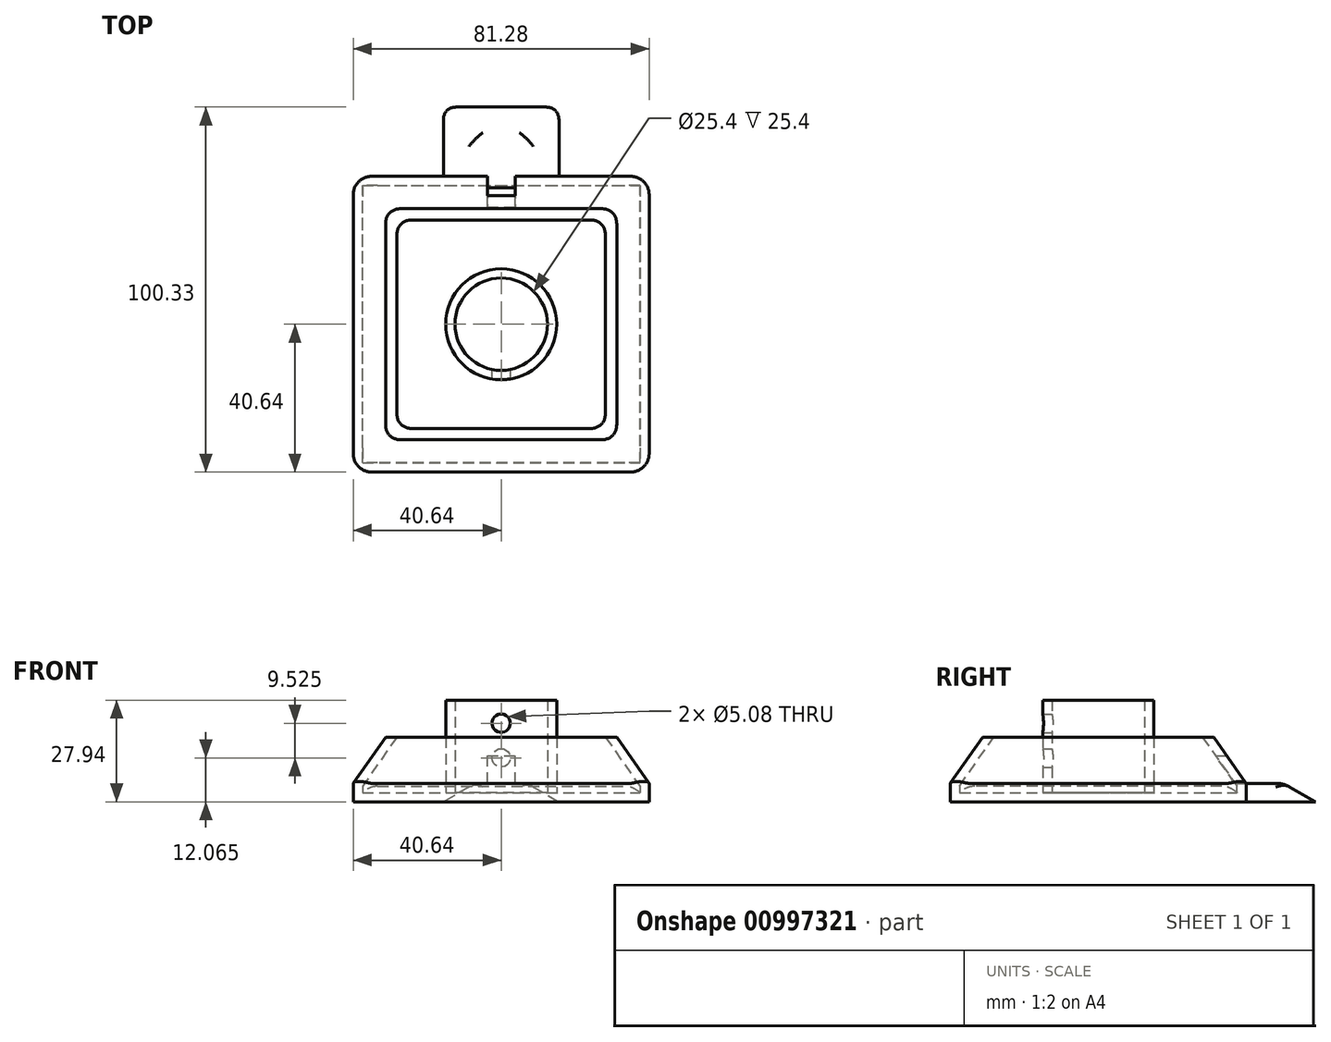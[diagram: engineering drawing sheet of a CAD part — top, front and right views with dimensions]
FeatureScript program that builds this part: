
annotation { "Feature Type Name" : "Feature", "Feature Type Description" : "" }
export const myFeature = defineFeature(function(context is Context, id is Id, definition is map)
    precondition{}
    {
        {
            var Q0;
            Q0=qCreatedBy(makeId("Top.planeOp"),FACE);
            var sketch = newSketch(context, id + "F0", { "sketchPlane" : qUnion([Q0])});
            skLineSegment(sketch, "E0.bottom", {"start": v(40.64, 40.64) * mm, "end": v(-40.64, 40.64) * mm});
            skLineSegment(sketch, "E0.top", {"start": v(40.64, -40.64) * mm, "end": v(-40.64, -40.64) * mm});
            skLineSegment(sketch, "E0.left", {"start": v(40.64, 40.64) * mm, "end": v(40.64, -40.64) * mm});
            skLineSegment(sketch, "E0.right", {"start": v(-40.64, 40.64) * mm, "end": v(-40.64, -40.64) * mm});
            skPoint(sketch, "E0.middle", {"position": v(0, 0) * mm});
            skSolve(sketch);
        }
        {
            var Q0;
            Q0 = qSketchRegion(id + "F0", true);
            extrude(context, id + "F1", {"entities" : qUnion([Q0]), "depth" : 5.08 * mm, "offsetDistance" : 25.4 * mm});
        }
        {
            var Q0;
            Q0=makeQuery(id+"F1.opExtrude","CAP_FACE",FACE,{"disambiguationData":[OSD([sQuery(id+"F0.wireOp",EDGE,"E0.bottom"),sQuery(id+"F0.wireOp",EDGE,"E0.top"),sQuery(id+"F0.wireOp",EDGE,"E0.left"),sQuery(id+"F0.wireOp",EDGE,"E0.right")])],"isStart":false});
            extrude(context, id + "F2", {"entities" : qUnion([Q0]), "operationType" : NewBodyOperationType.ADD, "depth" : 12.7 * mm, "offsetDistance" : 25.4 * mm, "hasDraft" : true, "draftAngle" : 35 * degree, "draftPullDirection" : true});
        }
        {
            var Q0;
            Q0=makeQuery(id+"F2.opExtrude","CAP_FACE",FACE,{"disambiguationData":[OSD([sQuery(id+"F0.wireOp",EDGE,"E0.bottom"),sQuery(id+"F0.wireOp",EDGE,"E0.top"),sQuery(id+"F0.wireOp",EDGE,"E0.left"),sQuery(id+"F0.wireOp",EDGE,"E0.right")])],"isStart":false});
            var Q1;
            Q1=makeQuery(id+"F1.opExtrude","CAP_FACE",FACE,{"disambiguationData":[OSD([sQuery(id+"F0.wireOp",EDGE,"E0.bottom"),sQuery(id+"F0.wireOp",EDGE,"E0.top"),sQuery(id+"F0.wireOp",EDGE,"E0.left"),sQuery(id+"F0.wireOp",EDGE,"E0.right")])],"isStart":true});
            shell(context, id + "F3", {"entities" : qUnion([Q0, Q1]), "thickness" : 2.54 * mm});
        }
        {
            var Q0;
            Q0=makeQuery(id+"F1.opExtrude","CAP_FACE",FACE,{"disambiguationData":[OSD([sQuery(id+"F0.wireOp",EDGE,"E0.bottom"),sQuery(id+"F0.wireOp",EDGE,"E0.top"),sQuery(id+"F0.wireOp",EDGE,"E0.left"),sQuery(id+"F0.wireOp",EDGE,"E0.right")])],"isStart":true});
            var sketch = newSketch(context, id + "F4", { "sketchPlane" : qUnion([Q0])});
            skLineSegment(sketch, "E1.0.0", {"start": v(40.64, 40.64) * mm, "end": v(-40.64, 40.64) * mm});
            skLineSegment(sketch, "E1.0.1", {"start": v(-40.64, 40.64) * mm, "end": v(-40.64, -40.64) * mm});
            skLineSegment(sketch, "E1.0.2", {"start": v(-40.64, -40.64) * mm, "end": v(40.64, -40.64) * mm});
            skLineSegment(sketch, "E1.0.3", {"start": v(40.64, -40.64) * mm, "end": v(40.64, 40.64) * mm});
            skSolve(sketch);
        }
        {
            var Q0;
            Q0 = qSketchRegion(id + "F4", true);
            extrude(context, id + "F5", {"entities" : qUnion([Q0]), "operationType" : NewBodyOperationType.ADD, "oppositeDirection" : true, "depth" : 2.54 * mm, "offsetDistance" : 25.4 * mm});
        }
        {
            var Q0;
            Q0=makeQuery(id+"F5.opExtrude","CAP_FACE",FACE,{"disambiguationData":[OSD([sQuery(id+"F4.wireOp",EDGE,"E1.0.0"),sQuery(id+"F4.wireOp",EDGE,"E1.0.1"),sQuery(id+"F4.wireOp",EDGE,"E1.0.2"),sQuery(id+"F4.wireOp",EDGE,"E1.0.3")])],"isStart":false});
            var sketch = newSketch(context, id + "F6", { "sketchPlane" : qUnion([Q0])});
            skCircle(sketch, "E2", {"center": v(0, 0) * mm, "radius": 12.7 * mm});
            skCircle(sketch, "E3.0", {"center": v(0, 0) * mm, "radius": 15.24 * mm});
            skSolve(sketch);
        }
        {
            var Q0;
            Q0 = qSketchRegion(id + "F6", true);
            extrude(context, id + "F7", {"entities" : qUnion([Q0]), "operationType" : NewBodyOperationType.ADD, "depth" : 25.4 * mm, "offsetDistance" : 25.4 * mm});
        }
        {
            var Q0;
            Q0=makeQuery(id+"F1.opExtrude","SWEPT_FACE",FACE,{"disambiguationData":[OSD([sQuery(id+"F0.wireOp",EDGE,"E0.bottom")])]});
            cPlane(context, id + "F8", {"entities" : qUnion([Q0]), "cplaneType" : CPlaneType.OFFSET, "offset" : 40.64 * mm, "oppositeDirection" : true, "width" : 152.4 * mm, "height" : 152.4 * mm});
        }
        {
            var Q0;
            Q0=qCreatedBy(id+"F8.planeOp",FACE);
            var sketch = newSketch(context, id + "F9", { "sketchPlane" : qUnion([Q0])});
            skCircle(sketch, "E4", {"center": v(0, 21.59) * mm, "radius": 2.54 * mm});
            skCircle(sketch, "E5", {"center": v(0, 12.07) * mm, "radius": 2.54 * mm});
            skSolve(sketch);
        }
        {
            var Q0;
            Q0 = qSketchRegion(id + "F9", true);
            extrude(context, id + "F10", {"entities" : qUnion([Q0]), "operationType" : NewBodyOperationType.REMOVE, "oppositeDirection" : true, "depth" : 17.78 * mm, "offsetDistance" : 25.4 * mm});
        }
        {
            var Q0;
            Q0=makeQuery(id+"F1.opExtrude","SWEPT_FACE",FACE,{"disambiguationData":[OSD([sQuery(id+"F0.wireOp",EDGE,"E0.bottom")])]});
            var sketch = newSketch(context, id + "F11", { "sketchPlane" : qUnion([Q0])});
            skLineSegment(sketch, "E6.bottom", {"start": v(3.81, 5.08) * mm, "end": v(-3.8, 5.08) * mm});
            skLineSegment(sketch, "E6.top", {"start": v(3.8, 12.7) * mm, "end": v(-3.81, 12.7) * mm});
            skLineSegment(sketch, "E6.left", {"start": v(3.81, 5.08) * mm, "end": v(3.8, 12.7) * mm});
            skLineSegment(sketch, "E6.right", {"start": v(-3.8, 5.08) * mm, "end": v(-3.81, 12.7) * mm});
            skPoint(sketch, "E6.middle", {"position": v(0, 8.9) * mm});
            skPoint(sketch, "E6.middle.positionSnap0", {"position": v(0, 5.08) * mm});
            skPoint(sketch, "E6.centerSnap0", {"position": v(0, 5.08) * mm});
            skSolve(sketch);
        }
        {
            var Q0;
            Q0 = qSketchRegion(id + "F11", true);
            extrude(context, id + "F12", {"entities" : qUnion([Q0]), "operationType" : NewBodyOperationType.REMOVE, "oppositeDirection" : true, "depth" : 12.7 * mm, "offsetDistance" : 25.4 * mm});
        }
        {
            var Q0;
            Q0=makeQuery(id+"F1.opExtrude","SWEPT_FACE",FACE,{"disambiguationData":[OSD([sQuery(id+"F0.wireOp",EDGE,"E0.bottom")])]});
            var sketch = newSketch(context, id + "F13", { "sketchPlane" : qUnion([Q0])});
            skLineSegment(sketch, "E7.bottom", {"start": v(15.88, 5.08) * mm, "end": v(-15.88, 5.08) * mm});
            skLineSegment(sketch, "E7.top", {"start": v(15.88, 0) * mm, "end": v(-15.88, 0) * mm});
            skLineSegment(sketch, "E7.left", {"start": v(15.88, 5.08) * mm, "end": v(15.88, 0) * mm});
            skLineSegment(sketch, "E7.right", {"start": v(-15.88, 5.08) * mm, "end": v(-15.88, 0) * mm});
            skPoint(sketch, "E7.middle", {"position": v(0, 2.54) * mm});
            skPoint(sketch, "E7.middle.positionSnap0", {"position": v(0, 5.08) * mm});
            skPoint(sketch, "E7.centerSnap0", {"position": v(0, 5.08) * mm});
            skSolve(sketch);
        }
        {
            var Q0;
            Q0 = qSketchRegion(id + "F13", true);
            extrude(context, id + "F14", {"entities" : qUnion([Q0]), "operationType" : NewBodyOperationType.ADD, "depth" : 19.05 * mm, "offsetDistance" : 25.4 * mm});
        }
        {
            var Q0;
            Q0=makeQuery(id+"F14.opExtrude","SWEPT_EDGE",EDGE,{"disambiguationData":[OSD([sQuery(id+"F0.wireOp",EDGE,"E0.bottom"),sQuery(id+"F13.wireOp",EDGE,"E7.bottom"),sQuery(id+"F13.wireOp",EDGE,"E7.right")])]});
            var Q1;
            Q1=makeQuery(id+"F14.opExtrude","CAP_EDGE",EDGE,{"disambiguationData":[OSD([sQuery(id+"F13.wireOp",EDGE,"E7.bottom")])],"isStart":false});
            var Q2;
            Q2=makeQuery(id+"F14.opExtrude","SWEPT_EDGE",EDGE,{"disambiguationData":[OSD([sQuery(id+"F0.wireOp",EDGE,"E0.bottom"),sQuery(id+"F13.wireOp",EDGE,"E7.bottom"),sQuery(id+"F13.wireOp",EDGE,"E7.left")])]});
            chamfer(context, id + "F15", {"entities" : qUnion([Q0, Q1, Q2]), "chamferType" : ChamferType.OFFSET_ANGLE, "width" : 5.08 * mm, "oppositeDirection" : false, "angle" : 60 * degree, "tangentPropagation" : true});
        }
        {
            var Q0;
            {var subQ0=sQuery(id+"F13.wireOp",EDGE,"E7.bottom");Q0=makeQuery(id+"F15.opChamfer","BLEND_EDGE",EDGE,{"blendedFrom":[makeQuery(id+"F14.opExtrude","SWEPT_EDGE",EDGE,{"disambiguationData":[OSD([sQuery(id+"F0.wireOp",EDGE,"E0.bottom"),subQ0,sQuery(id+"F13.wireOp",EDGE,"E7.right")])]}),makeQuery(id+"F14.boolean.opBoolean","MERGE",FACE,{"derivedFrom":[makeQuery(id+"F12.boolean.opBoolean","COPY",FACE,{"derivedFrom":makeQuery(id+"F12.opExtrude","SWEPT_FACE",FACE,{"disambiguationData":[OSD([sQuery(id+"F11.wireOp",EDGE,"E6.bottom")])]})}),makeQuery(id+"F14.opExtrude","SWEPT_FACE",FACE,{"disambiguationData":[OSD([subQ0])]})]})],"blendedInto":[makeQuery(id+"F14.boolean.opBoolean","MERGE",FACE,{"derivedFrom":[makeQuery(id+"F12.boolean.opBoolean","COPY",FACE,{"derivedFrom":makeQuery(id+"F12.opExtrude","SWEPT_FACE",FACE,{"disambiguationData":[OSD([sQuery(id+"F11.wireOp",EDGE,"E6.bottom")])]})}),makeQuery(id+"F14.opExtrude","SWEPT_FACE",FACE,{"disambiguationData":[OSD([subQ0])]})]})]});}
            var Q1;
            {var subQ0=sQuery(id+"F13.wireOp",EDGE,"E7.bottom");Q1=makeQuery(id+"F15.opChamfer","BLEND_EDGE",EDGE,{"blendedFrom":[makeQuery(id+"F14.opExtrude","CAP_EDGE",EDGE,{"disambiguationData":[OSD([subQ0])],"isStart":false}),makeQuery(id+"F14.boolean.opBoolean","MERGE",FACE,{"derivedFrom":[makeQuery(id+"F12.boolean.opBoolean","COPY",FACE,{"derivedFrom":makeQuery(id+"F12.opExtrude","SWEPT_FACE",FACE,{"disambiguationData":[OSD([sQuery(id+"F11.wireOp",EDGE,"E6.bottom")])]})}),makeQuery(id+"F14.opExtrude","SWEPT_FACE",FACE,{"disambiguationData":[OSD([subQ0])]})]})],"blendedInto":[makeQuery(id+"F14.boolean.opBoolean","MERGE",FACE,{"derivedFrom":[makeQuery(id+"F12.boolean.opBoolean","COPY",FACE,{"derivedFrom":makeQuery(id+"F12.opExtrude","SWEPT_FACE",FACE,{"disambiguationData":[OSD([sQuery(id+"F11.wireOp",EDGE,"E6.bottom")])]})}),makeQuery(id+"F14.opExtrude","SWEPT_FACE",FACE,{"disambiguationData":[OSD([subQ0])]})]})]});}
            var Q2;
            {var subQ0=sQuery(id+"F13.wireOp",EDGE,"E7.bottom");Q2=makeQuery(id+"F15.opChamfer","BLEND_EDGE",EDGE,{"blendedFrom":[makeQuery(id+"F14.opExtrude","SWEPT_EDGE",EDGE,{"disambiguationData":[OSD([sQuery(id+"F0.wireOp",EDGE,"E0.bottom"),subQ0,sQuery(id+"F13.wireOp",EDGE,"E7.left")])]}),makeQuery(id+"F14.boolean.opBoolean","MERGE",FACE,{"derivedFrom":[makeQuery(id+"F12.boolean.opBoolean","COPY",FACE,{"derivedFrom":makeQuery(id+"F12.opExtrude","SWEPT_FACE",FACE,{"disambiguationData":[OSD([sQuery(id+"F11.wireOp",EDGE,"E6.bottom")])]})}),makeQuery(id+"F14.opExtrude","SWEPT_FACE",FACE,{"disambiguationData":[OSD([subQ0])]})]})],"blendedInto":[makeQuery(id+"F14.boolean.opBoolean","MERGE",FACE,{"derivedFrom":[makeQuery(id+"F12.boolean.opBoolean","COPY",FACE,{"derivedFrom":makeQuery(id+"F12.opExtrude","SWEPT_FACE",FACE,{"disambiguationData":[OSD([sQuery(id+"F11.wireOp",EDGE,"E6.bottom")])]})}),makeQuery(id+"F14.opExtrude","SWEPT_FACE",FACE,{"disambiguationData":[OSD([subQ0])]})]})]});}
            var Q3;
            {var subQ0=sQuery(id+"F13.wireOp",EDGE,"E7.bottom");Q3=makeQuery(id+"F15.opChamfer","BLEND_EDGE",EDGE,{"blendedFrom":[makeQuery(id+"F14.opExtrude","SWEPT_EDGE",EDGE,{"disambiguationData":[OSD([sQuery(id+"F0.wireOp",EDGE,"E0.bottom"),subQ0,sQuery(id+"F13.wireOp",EDGE,"E7.right")])]}),makeQuery(id+"F14.opExtrude","CAP_EDGE",EDGE,{"disambiguationData":[OSD([subQ0])],"isStart":false})],"blendedInto":[]});}
            var Q4;
            {var subQ0=sQuery(id+"F13.wireOp",EDGE,"E7.bottom");Q4=makeQuery(id+"F15.opChamfer","BLEND_EDGE",EDGE,{"blendedFrom":[makeQuery(id+"F14.opExtrude","SWEPT_EDGE",EDGE,{"disambiguationData":[OSD([sQuery(id+"F0.wireOp",EDGE,"E0.bottom"),subQ0,sQuery(id+"F13.wireOp",EDGE,"E7.left")])]}),makeQuery(id+"F14.opExtrude","CAP_EDGE",EDGE,{"disambiguationData":[OSD([subQ0])],"isStart":false})],"blendedInto":[]});}
            fillet(context, id + "F16", {"entities" : qUnion([Q0, Q1, Q2, Q3, Q4]), "radius" : 7.62 * mm, "tangentPropagation" : true, "allowEdgeOverflow" : false});
        }
        {
            var Q0;
            Q0=makeQuery(id+"F2.opExtrude","SWEPT_EDGE",EDGE,{"disambiguationData":[OSD([sQuery(id+"F0.wireOp",EDGE,"E0.bottom"),sQuery(id+"F0.wireOp",EDGE,"E0.right")])]});
            var Q1;
            Q1=makeQuery(id+"F1.opExtrude","SWEPT_EDGE",EDGE,{"disambiguationData":[OSD([sQuery(id+"F0.wireOp",EDGE,"E0.bottom"),sQuery(id+"F0.wireOp",EDGE,"E0.right")])]});
            var Q2;
            Q2=makeQuery(id+"F1.opExtrude","SWEPT_EDGE",EDGE,{"disambiguationData":[OSD([sQuery(id+"F0.wireOp",EDGE,"E0.top"),sQuery(id+"F0.wireOp",EDGE,"E0.right")])]});
            var Q3;
            Q3=makeQuery(id+"F2.opExtrude","SWEPT_EDGE",EDGE,{"disambiguationData":[OSD([sQuery(id+"F0.wireOp",EDGE,"E0.top"),sQuery(id+"F0.wireOp",EDGE,"E0.right")])]});
            var Q4;
            Q4=makeQuery(id+"F1.opExtrude","SWEPT_EDGE",EDGE,{"disambiguationData":[OSD([sQuery(id+"F0.wireOp",EDGE,"E0.top"),sQuery(id+"F0.wireOp",EDGE,"E0.left")])]});
            var Q5;
            Q5=makeQuery(id+"F2.opExtrude","SWEPT_EDGE",EDGE,{"disambiguationData":[OSD([sQuery(id+"F0.wireOp",EDGE,"E0.top"),sQuery(id+"F0.wireOp",EDGE,"E0.left")])]});
            var Q6;
            Q6=makeQuery(id+"F2.opExtrude","SWEPT_EDGE",EDGE,{"disambiguationData":[OSD([sQuery(id+"F0.wireOp",EDGE,"E0.bottom"),sQuery(id+"F0.wireOp",EDGE,"E0.left")])]});
            var Q7;
            Q7=makeQuery(id+"F1.opExtrude","SWEPT_EDGE",EDGE,{"disambiguationData":[OSD([sQuery(id+"F0.wireOp",EDGE,"E0.bottom"),sQuery(id+"F0.wireOp",EDGE,"E0.left")])]});
            fillet(context, id + "F17", {"entities" : qUnion([Q0, Q1, Q2, Q3, Q4, Q5, Q6, Q7]), "radius" : 5.08 * mm, "tangentPropagation" : true, "allowEdgeOverflow" : false});
        }
        {
            var Q0;
            {var subQ0=sQuery(id+"F0.wireOp",EDGE,"E0.right");var subQ1=sQuery(id+"F0.wireOp",EDGE,"E0.bottom");Q0=makeQuery(id+"F3.opShell","OFFSET_EDGE",EDGE,{"disambiguationData":[OSD([subQ1,subQ0]),TDD([makeQuery(id+"F2.opExtrude","SWEPT_EDGE",EDGE,{"disambiguationData":[OSD([subQ1,subQ0])]})])]});}
            var Q1;
            {var subQ0=sQuery(id+"F0.wireOp",EDGE,"E0.left");var subQ1=sQuery(id+"F0.wireOp",EDGE,"E0.bottom");Q1=makeQuery(id+"F3.opShell","OFFSET_EDGE",EDGE,{"disambiguationData":[OSD([subQ1,subQ0]),TDD([makeQuery(id+"F2.opExtrude","SWEPT_EDGE",EDGE,{"disambiguationData":[OSD([subQ1,subQ0])]})])]});}
            var Q2;
            {var subQ0=sQuery(id+"F0.wireOp",EDGE,"E0.left");var subQ1=sQuery(id+"F0.wireOp",EDGE,"E0.top");Q2=makeQuery(id+"F3.opShell","OFFSET_EDGE",EDGE,{"disambiguationData":[OSD([subQ1,subQ0]),TDD([makeQuery(id+"F2.opExtrude","SWEPT_EDGE",EDGE,{"disambiguationData":[OSD([subQ1,subQ0])]})])]});}
            var Q3;
            {var subQ0=sQuery(id+"F0.wireOp",EDGE,"E0.right");var subQ1=sQuery(id+"F0.wireOp",EDGE,"E0.top");Q3=makeQuery(id+"F3.opShell","OFFSET_EDGE",EDGE,{"disambiguationData":[OSD([subQ1,subQ0]),TDD([makeQuery(id+"F2.opExtrude","SWEPT_EDGE",EDGE,{"disambiguationData":[OSD([subQ1,subQ0])]})])]});}
            fillet(context, id + "F18", {"entities" : qUnion([Q0, Q1, Q2, Q3]), "radius" : 5.08 * mm, "tangentPropagation" : true, "allowEdgeOverflow" : false});
        }
    });
